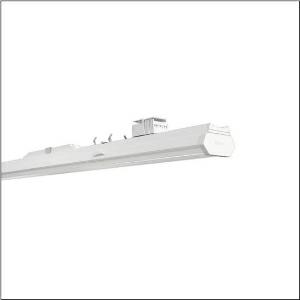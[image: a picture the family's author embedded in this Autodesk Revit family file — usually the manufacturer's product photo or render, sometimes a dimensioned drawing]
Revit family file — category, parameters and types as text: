
# Revit family: licross_r__11_protected_ho_51tp11dn4exrd_8d0d
name_source: partatom
category: Lighting Fixtures
units: mm (PartAtom-declared; Revit-internal decimal feet)

## family parameters
Cut with Voids When Loaded = No
Host = Face
Light Source = No
Part Type = Normal
Room Calculation Point = No
Round Connector Dimension = Use Diameter
Shared = No

## types (1)
- --- (1 x LED, 2210 lm, 14.3 W, 4000K)
    Apparent Load = 14 VA
    CIE Flux Codes = 84 94 98 99 100
    Color Rendering = 80
    Color Temperature = 4000K
    Default Elevation = 1800 mm
    Description = Licross® 11 Protected HOluminaire insert, length: 1.500mm, width: 90mm, height: 101mm, LED rated luminous flux: 14.140lm, light colour: 840, control gear: DALI 2, control gear: ECG DALI, with plug, 6-pole, with phase selection, mains connection: 220..240V, AC/DC, 0/50..60Hz, without changeover relay, for emergency light function, for central battery installations according to DIN EN 60598-2-22, halogen-free wiring, primary optical cover: cover, of PMMA, light emission: direct with ceiling illumination distribution, protection rating (complete): IP64, insulation class (complete): insulation class I (protective earthing), certification: CE, ENEC, VDE, protection symbol: D if used in an environment without relevant dust loads with corresponding accessories, permissible ambient temperature for indoor applications: -25..+35°C, standard: EN 60598-2-22, reducing of maximum allowable ambient temperature of 5°C with ceiling mounting, corresponds to IFS (International Featured Standards) requirements for safety and quality in the food industry, packaging unit: 1 piece
    Height = 92 mm
    Lamp = 1 x LED
    Lamp Light Flux = 2210 lm
    Lamp Power = 14.3 W
    Lamp count = 1
    Length = 1500 mm
    Luminous efficacy = 155 lm/W
    Manufacturer = Siteco
    ModVariant = No
    Model = 51TP11DN4EXRD
    Mounting Place = Ceiling
    Mounting Type = Pendant
    Number of Poles = 1
    OnlyDefault = Yes
    Power Factor = 1
    Product Name = Licross® 11 Protected HO
    Product group = luminaire insert
    ProductGroupID = 902
    Protection Class = Protection class I
    Protection Degree = IP 64
    RLX_Detail_Level = 1
    RlxData = <blob elided: 24269 chars, md5=921791d2>
    Socket = socket
    Standby Power = 0 W
    System Light Flux = 2210 lm
    System Power = 14 W
    Type Comments = : DC mode (central or group accumulator) initial emergency light level
    Type Image = l_1256148.jpg
    URL = http://relux.com
    VarID = @adj_134649
    Voltage = 0 V
    Weight = 0.00 kg
    Width = 88 mm

## geometry (parser evidence)
native form markers: Blend x4, Sweep x11
no freeform markers — native parametric forms only
